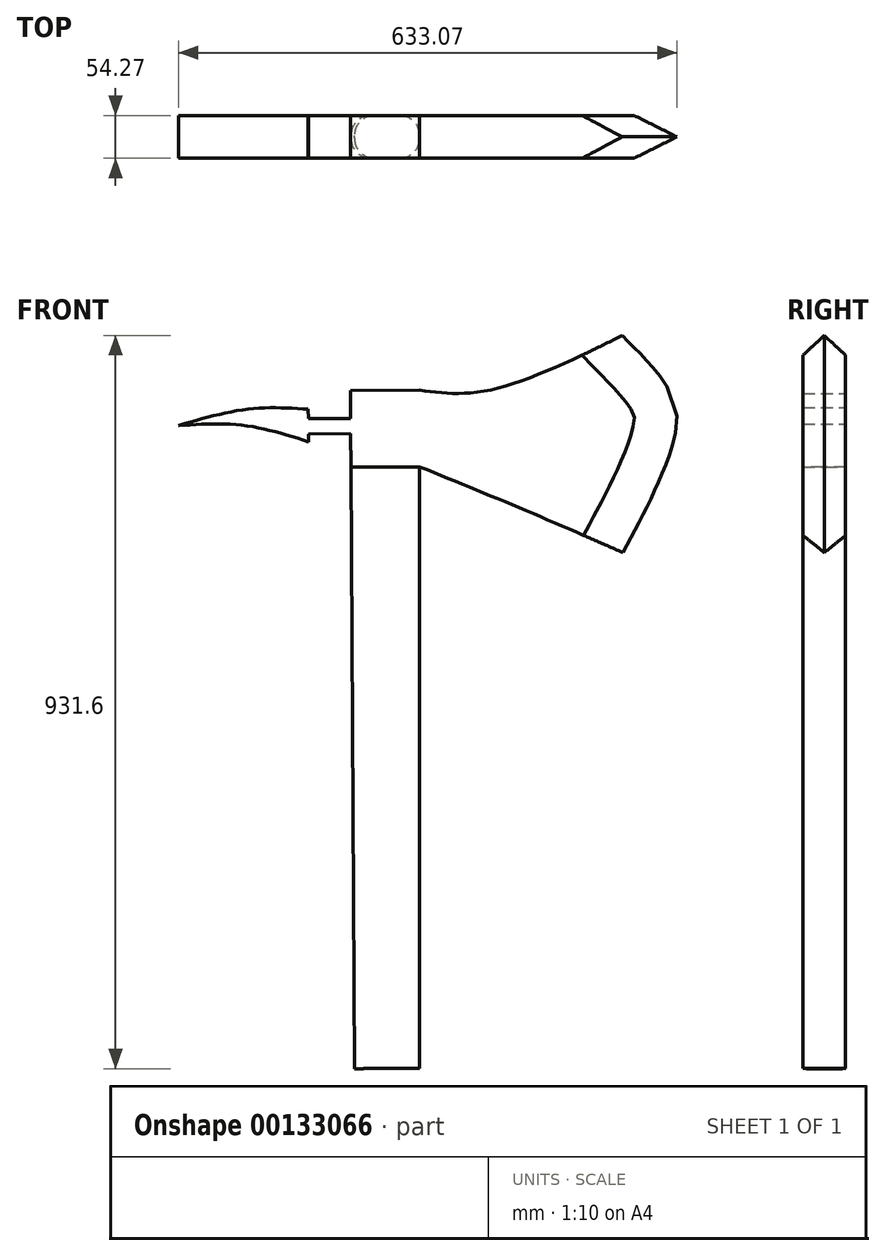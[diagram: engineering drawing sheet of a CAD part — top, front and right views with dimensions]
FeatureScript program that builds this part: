
annotation { "Feature Type Name" : "Feature", "Feature Type Description" : "" }
export const myFeature = defineFeature(function(context is Context, id is Id, definition is map)
    precondition{}
    {
        {
            var Q0;
            Q0=qCreatedBy(makeId("Front.planeOp"),FACE);
            var sketch = newSketch(context, id + "F0", { "sketchPlane" : qUnion([Q0])});
            skLineSegment(sketch, "E0", {"start": v(-147.7, 431.1) * mm, "end": v(-235.19, 430.54) * mm});
            skLineSegment(sketch, "E1", {"start": v(-235.19, 430.54) * mm, "end": v(-235.8, 527.89) * mm});
            skLineSegment(sketch, "E2", {"start": v(-235.8, 527.89) * mm, "end": v(-147.7, 528.45) * mm});
            skLineSegment(sketch, "E3", {"start": v(-147.7, 528.45) * mm, "end": v(-147.7, 431.1) * mm});
            skFitSpline(sketch, "E4", {"points": [v(-147.7, 528.45) * mm, v(-59.66, 528.45) * mm, v(153.76, 620.65) * mm], "startDerivative": vector(209.46, -28.37) * mm, "endDerivative": vector(379.93, 195.04) * mm});
            skFitSpline(sketch, "E5", {"points": [v(153.76, 620.65) * mm, v(225.67, 506.98) * mm, v(153.76, 302.84) * mm], "startDerivative": vector(227.44, -234.23) * mm, "endDerivative": vector(-210.17, -395.05) * mm});
            skFitSpline(sketch, "E6", {"points": [v(-147.7, 431.1) * mm, v(0, 370.11) * mm, v(153.76, 302.84) * mm], "startDerivative": vector(297.9, -121.15) * mm, "endDerivative": vector(304.98, -135.3) * mm});
            skLineSegment(sketch, "E7", {"start": v(-289.32, 504.35) * mm, "end": v(-289.06, 462.86) * mm});
            skPoint(sketch, "E8.2.internal.snap0", {"position": v(-289.2, 483.6) * mm});
            skFitSpline(sketch, "E8", {"points": [v(-289.32, 504.35) * mm, v(-365.88, 504.35) * mm, v(-454.03, 483.6) * mm], "startDerivative": vector(-157.57, 9.54) * mm, "endDerivative": vector(-171.65, -50.2) * mm});
            skFitSpline(sketch, "E9", {"points": [v(-454.03, 483.6) * mm, v(-370.52, 483.6) * mm, v(-289.06, 462.86) * mm], "startDerivative": vector(168.46, 10.34) * mm, "endDerivative": vector(161.49, -51.8) * mm});
            skPoint(sketch, "E10.endSnap0", {"position": v(-235.5, 479.21) * mm});
            skLineSegment(sketch, "E11", {"start": v(-289.25, 492.24) * mm, "end": v(-235.5, 492.58) * mm});
            skLineSegment(sketch, "E12", {"start": v(-289.12, 472.99) * mm, "end": v(-235.46, 473.33) * mm});
            skSolve(sketch);
        }
        {
            var Q0;
            Q0=qCreatedBy(makeId("Front.planeOp"),FACE);
            var sketch = newSketch(context, id + "F1", { "sketchPlane" : qUnion([Q0])});
            skLineSegment(sketch, "E13", {"start": v(-235.17, 430.54) * mm, "end": v(-230.6, -333.47) * mm});
            skLineSegment(sketch, "E14", {"start": v(-230.6, -333.47) * mm, "end": v(-147.72, -332.98) * mm});
            skLineSegment(sketch, "E15", {"start": v(-235.17, 430.54) * mm, "end": v(-147.72, 431.07) * mm});
            skLineSegment(sketch, "E16", {"start": v(-147.72, 431.07) * mm, "end": v(-147.72, -332.98) * mm});
            skSolve(sketch);
        }
        {
            var Q0;
            Q0 = qSketchRegion(id + "F0", true);
            var Q1;
            Q1 = qSketchRegion(id + "F1", true);
            extrude(context, id + "F2", {"entities" : qUnion([Q0, Q1]), "depth" : 54.27 * mm});
        }
        {
            var Q0;
            Q0=makeQuery(id+"F2.opExtrude","CAP_EDGE",EDGE,{"disambiguationData":[OSD([sQuery(id+"F1.wireOp",EDGE,"E13")])],"isStart":false});
            var Q1;
            Q1=makeQuery(id+"F2.opExtrude","CAP_EDGE",EDGE,{"disambiguationData":[OSD([sQuery(id+"F1.wireOp",EDGE,"E16")])],"isStart":false});
            var Q2;
            Q2=makeQuery(id+"F2.opExtrude","CAP_EDGE",EDGE,{"disambiguationData":[OSD([sQuery(id+"F1.wireOp",EDGE,"E13")])],"isStart":true});
            var Q3;
            Q3=makeQuery(id+"F2.opExtrude","CAP_EDGE",EDGE,{"disambiguationData":[OSD([sQuery(id+"F1.wireOp",EDGE,"E16")])],"isStart":true});
            fillet(context, id + "F3", {"entities" : qUnion([Q0, Q1, Q2, Q3]), "radius" : 25.4 * mm, "tangentPropagation" : true, "allowEdgeOverflow" : false});
        }
        {
            var Q0;
            Q0=makeQuery(id+"F2.opExtrude","CAP_EDGE",EDGE,{"disambiguationData":[OSD([sQuery(id+"F0.wireOp",EDGE,"E5")])],"isStart":true});
            var Q1;
            Q1=makeQuery(id+"F2.opExtrude","CAP_EDGE",EDGE,{"disambiguationData":[OSD([sQuery(id+"F0.wireOp",EDGE,"E5")])],"isStart":false});
            chamfer(context, id + "F4", {"entities" : qUnion([Q0, Q1]), "chamferType" : ChamferType.TWO_OFFSETS, "width1" : 50.8 * mm, "oppositeDirection" : true, "width2" : 101.6 * mm, "tangentPropagation" : true});
        }
    });
